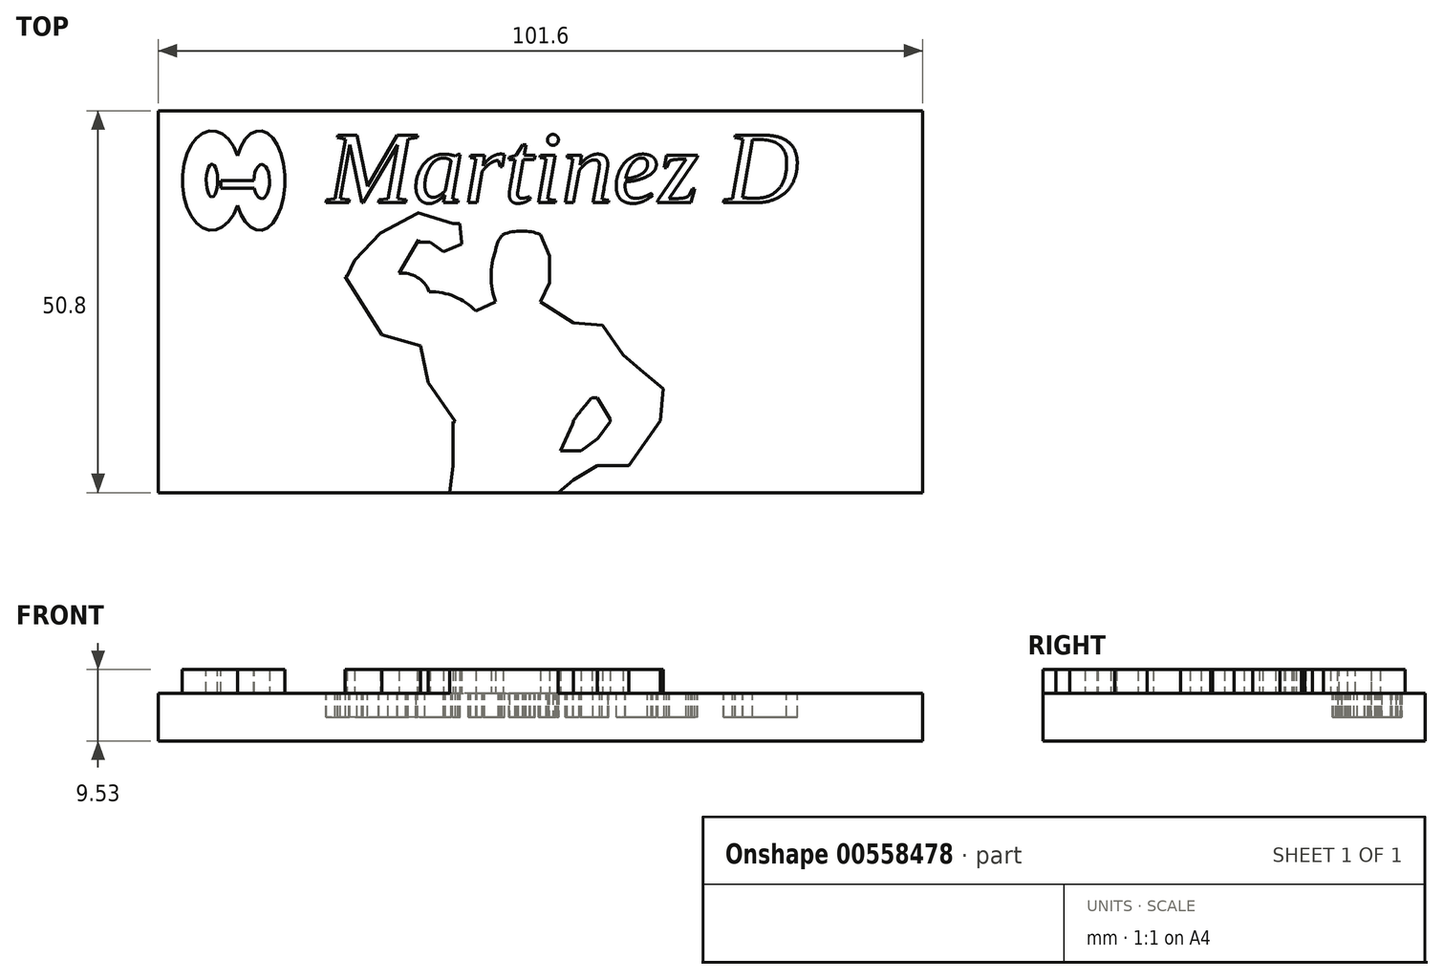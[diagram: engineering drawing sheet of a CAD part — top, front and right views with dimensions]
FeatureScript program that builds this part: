
annotation { "Feature Type Name" : "Feature", "Feature Type Description" : "" }
export const myFeature = defineFeature(function(context is Context, id is Id, definition is map)
    precondition{}
    {
        {
            var Q0;
            Q0=qCreatedBy(makeId("Top.planeOp"),FACE);
            var sketch = newSketch(context, id + "F0", { "sketchPlane" : qUnion([Q0])});
            skLineSegment(sketch, "E0.top", {"start": v(50.8, -25.4) * mm, "end": v(-50.8, -25.4) * mm});
            skLineSegment(sketch, "E0.left", {"start": v(50.8, 25.4) * mm, "end": v(50.8, -25.4) * mm});
            skLineSegment(sketch, "E0.right", {"start": v(-50.8, 25.4) * mm, "end": v(-50.8, -25.4) * mm});
            skPoint(sketch, "E0.middle", {"position": v(0, 0) * mm});
            skLineSegment(sketch, "E1", {"start": v(-50.8, 25.4) * mm, "end": v(29.22, 25.4) * mm});
            skLineSegment(sketch, "E2", {"start": v(29.22, 25.4) * mm, "end": v(50.8, 25.4) * mm});
            skSolve(sketch);
        }
        {
            var Q0;
            Q0=makeQuery(id+"F0.imprint","IMPRINT",FACE,{"disambiguationData":[TD([[makeQuery(id+"F0.imprint","IMPRINT",EDGE,{"derivedFrom":sQuery(id+"F0.wireOp",EDGE,"E0.top")}),-1.0]])]});
            extrude(context, id + "F1", {"entities" : qUnion([Q0]), "depth" : 6.35 * mm, "offsetDistance" : 25.4 * mm});
        }
        {
            var Q0;
            Q0=makeQuery(id+"F1.opExtrude","CAP_FACE",FACE,{"disambiguationData":[OSD([sQuery(id+"F0.wireOp",EDGE,"E0.top"),sQuery(id+"F0.wireOp",EDGE,"E0.left"),sQuery(id+"F0.wireOp",EDGE,"E0.right"),sQuery(id+"F0.wireOp",EDGE,"E1"),sQuery(id+"F0.wireOp",EDGE,"E2")])],"isStart":false});
            var sketch = newSketch(context, id + "F2", { "sketchPlane" : qUnion([Q0])});
            skPoint(sketch, "E3.centerSnap0", {"position": v(-40.78, 16.13) * mm});
            skPoint(sketch, "E3.center.orphan", {"position": v(-37.34, 16.13) * mm});
            skEllipticalArc(sketch, "E4", {});
            skEllipticalArc(sketch, "E5", {});
            skEllipse(sketch, "E6", {"center": v(-43.67, 16.13) * mm, "majorRadius": 4.6 * mm, "minorRadius": 1.55 * mm, "majorAxis": v(0, -1)});
            skEllipse(sketch, "E7", {"center": v(-37.34, 16.13) * mm, "majorRadius": 4.03 * mm, "minorRadius": 1.4 * mm, "majorAxis": v(0, -1)});
            const initialGuessF2  = {"E4": [-0.04366867616772652, 0.016128746792674065, 0, -1, 0.006619533523917198, 0.00393258710358012, 2.0939321384810903, 1.0476605151087033], "E5": [-0.03733694925904274, 0.016128746792674065, 0, -1, 0.006619533523917198, 0.003376708431436235, 5.235524792070883, 4.189253168698496]};
            skSetInitialGuess(sketch, initialGuessF2);
            skSolve(sketch);
        }
        {
            var Q0;
            Q0=makeQuery(id+"F2.imprint","IMPRINT",FACE,{"disambiguationData":[TD([[makeQuery(id+"F2.imprint","IMPRINT",EDGE,{"derivedFrom":sQuery(id+"F2.wireOp",EDGE,"E6")}),-1.0]])]});
            var Q1;
            Q1=makeQuery(id+"F2.imprint","IMPRINT",FACE,{"disambiguationData":[TD([[makeQuery(id+"F2.imprint","IMPRINT",EDGE,{"derivedFrom":sQuery(id+"F2.wireOp",EDGE,"E7")}),-1.0]])]});
            var Q2;
            Q2=makeQuery(id+"F2.imprint","IMPRINT",FACE,{"disambiguationData":[TD([[makeQuery(id+"F2.imprint","IMPRINT",EDGE,{"derivedFrom":sQuery(id+"F2.wireOp",EDGE,"E7")}),1.0]])]});
            var Q3;
            Q3=makeQuery(id+"F2.imprint","IMPRINT",FACE,{"disambiguationData":[TD([[makeQuery(id+"F2.imprint","IMPRINT",EDGE,{"derivedFrom":sQuery(id+"F2.wireOp",EDGE,"E6")}),1.0]])]});
            extrude(context, id + "F3", {"entities" : qUnion([Q0, Q1, Q2, Q3]), "operationType" : NewBodyOperationType.ADD, "depth" : 3.17 * mm, "offsetDistance" : 25.4 * mm});
        }
        {
            var Q0;
            Q0=makeQuery(id+"F3.opExtrude","CAP_FACE",FACE,{"disambiguationData":[OSD([sQuery(id+"F2.wireOp",EDGE,"E4"),sQuery(id+"F2.wireOp",EDGE,"E5")])],"isStart":false});
            var sketch = newSketch(context, id + "F4", { "sketchPlane" : qUnion([Q0])});
            skEllipse(sketch, "E8", {"center": v(-43.67, 16.13) * mm, "majorRadius": 2.17 * mm, "minorRadius": 0.76 * mm, "majorAxis": v(0, -1)});
            skEllipse(sketch, "E9", {"center": v(-37.05, 15.99) * mm, "majorRadius": 2.27 * mm, "minorRadius": 1.05 * mm, "majorAxis": v(0, -1)});
            skSolve(sketch);
        }
        {
            var Q0;
            Q0=makeQuery(id+"F4.imprint","IMPRINT",FACE,{"disambiguationData":[TD([[makeQuery(id+"F4.imprint","IMPRINT",EDGE,{"derivedFrom":sQuery(id+"F4.wireOp",EDGE,"E9")}),1.0]])]});
            var Q1;
            Q1=makeQuery(id+"F4.imprint","IMPRINT",FACE,{"disambiguationData":[TD([[makeQuery(id+"F4.imprint","IMPRINT",EDGE,{"derivedFrom":sQuery(id+"F4.wireOp",EDGE,"E8")}),1.0]])]});
            extrude(context, id + "F5", {"entities" : qUnion([Q0, Q1]), "operationType" : NewBodyOperationType.REMOVE, "oppositeDirection" : true, "depth" : 3.17 * mm, "offsetDistance" : 25.4 * mm});
        }
        {
            var Q0;
            Q0=makeQuery(id+"F3.opExtrude","CAP_FACE",FACE,{"disambiguationData":[OSD([sQuery(id+"F2.wireOp",EDGE,"E4"),sQuery(id+"F2.wireOp",EDGE,"E5")])],"isStart":false});
            var sketch = newSketch(context, id + "F6", { "sketchPlane" : qUnion([Q0])});
            skLineSegment(sketch, "E10.bottom", {"start": v(-42.91, 16.13) * mm, "end": v(-38.02, 16.13) * mm});
            skLineSegment(sketch, "E10.top", {"start": v(-42.91, 15.09) * mm, "end": v(-38.02, 15.09) * mm});
            skLineSegment(sketch, "E10.right", {"start": v(-38.02, 16.13) * mm, "end": v(-38.02, 15.09) * mm});
            skLineSegment(sketch, "E11", {"start": v(-42.5, 16.13) * mm, "end": v(-42.5, 15.09) * mm});
            skSolve(sketch);
        }
        {
            var Q0;
            {var subQ0=sQuery(id+"F6.wireOp",EDGE,"E11");Q0=makeQuery(id+"F6.imprint","IMPRINT",FACE,{"disambiguationData":[TD([[makeQuery(id+"F6.imprint","IMPRINT",EDGE,{"derivedFrom":subQ0}),1.0]])]});}
            extrude(context, id + "F7", {"entities" : qUnion([Q0]), "operationType" : NewBodyOperationType.REMOVE, "oppositeDirection" : true, "depth" : 3.17 * mm, "offsetDistance" : 25.4 * mm});
        }
        {
            var Q0;
            Q0=makeQuery(id+"F1.opExtrude","CAP_FACE",FACE,{"disambiguationData":[OSD([sQuery(id+"F0.wireOp",EDGE,"E0.top"),sQuery(id+"F0.wireOp",EDGE,"E0.left"),sQuery(id+"F0.wireOp",EDGE,"E0.right"),sQuery(id+"F0.wireOp",EDGE,"E1"),sQuery(id+"F0.wireOp",EDGE,"E2")])],"isStart":false});
            var sketch = newSketch(context, id + "F8", { "sketchPlane" : qUnion([Q0])});
            skText(sketch, "E12", { "text": "Martinez D ", "fontName": "Tinos-Italic.ttf"});
            const initialGuessF8  = {"E12": [-0.02836, 0.0132, 1, 0, 0.00985]};
            skSetInitialGuess(sketch, initialGuessF8);
            skSolve(sketch);
        }
        {
            var Q0;
            Q0 = qSketchRegion(id + "F8", true);
            extrude(context, id + "F9", {"entities" : qUnion([Q0]), "operationType" : NewBodyOperationType.REMOVE, "oppositeDirection" : true, "depth" : 3.17 * mm, "offsetDistance" : 25.4 * mm});
        }
        {
            var Q0;
            {var subQ0=sQuery(id+"F0.wireOp",EDGE,"E2");var subQ1=sQuery(id+"F0.wireOp",EDGE,"E1");var subQ2=sQuery(id+"F0.wireOp",EDGE,"E0.right");var subQ3=sQuery(id+"F0.wireOp",EDGE,"E0.left");var subQ4=sQuery(id+"F0.wireOp",EDGE,"E0.top");Q0=makeQuery(id+"F9.boolean.opBoolean","SPLIT",FACE,{"disambiguationData":[TD([makeQuery(id+"F1.opExtrude","SWEPT_FACE",FACE,{"disambiguationData":[OSD([subQ4])]})])],"derivedFrom":makeQuery(id+"F1.opExtrude","CAP_FACE",FACE,{"disambiguationData":[OSD([subQ4,subQ3,subQ2,subQ1,subQ0])],"isStart":false})});}
            var sketch = newSketch(context, id + "F10", { "sketchPlane" : qUnion([Q0])});
            skArc(sketch, "E13", {"start": v(-14.77, 1.35) * mm, "mid": v(-16.37, 3.25) * mm, "end": v(-18.8, 3.8) * mm});
            skArc(sketch, "E14", {"start": v(-8.58, -1.24) * mm, "mid": v(-11.4, 0.7) * mm, "end": v(-14.77, 1.35) * mm});
            skPoint(sketch, "E15.1.internal.orphan", {"position": v(-6, 0) * mm});
            skArc(sketch, "E16", {"start": v(-6, 6.82) * mm, "mid": v(-6.55, 3.4) * mm, "end": v(-6, 0) * mm});
            skArc(sketch, "E17", {"start": v(-4.99, 8.97) * mm, "mid": v(-5.63, 7.96) * mm, "end": v(-6, 6.82) * mm});
            skPoint(sketch, "E18.end.orphan", {"position": v(0, 8.97) * mm});
            skArc(sketch, "E19", {"start": v(0, 8.97) * mm, "mid": v(-2.5, 9.4) * mm, "end": v(-4.99, 8.97) * mm});
            skFitSpline(sketch, "E20", {"points": [v(-12.04, -25.4) * mm, v(-11.6, -21.82) * mm], "startDerivative": vector(0.43, 3.58) * mm, "endDerivative": vector(0.43, 3.58) * mm});
            skFitSpline(sketch, "E21", {"points": [v(-11.6, -21.82) * mm, v(-11.6, -15.92) * mm], "startDerivative": vector(0, 5.9) * mm, "endDerivative": vector(0, 5.9) * mm});
            skFitSpline(sketch, "E22", {"points": [v(-11.32, -15.92) * mm, v(-14.91, -10.74) * mm], "startDerivative": vector(-3.6, 5.18) * mm, "endDerivative": vector(-3.6, 5.18) * mm});
            skFitSpline(sketch, "E23", {"points": [v(-14.91, -10.74) * mm, v(-15.92, -5.85) * mm], "startDerivative": vector(-1, 4.9) * mm, "endDerivative": vector(-1, 4.9) * mm});
            skFitSpline(sketch, "E24", {"points": [v(-15.92, -5.85) * mm, v(-21.1, -4.4) * mm], "startDerivative": vector(-5.18, 1.44) * mm, "endDerivative": vector(-5.18, 1.44) * mm});
            skFitSpline(sketch, "E25", {"points": [v(-21.1, -4.4) * mm, v(-25.99, 3.36) * mm], "startDerivative": vector(-4.88, 7.77) * mm, "endDerivative": vector(-4.88, 7.77) * mm});
            skFitSpline(sketch, "E26", {"points": [v(-25.7, 3.36) * mm, v(-24.7, 5.52) * mm], "startDerivative": vector(1, 2.16) * mm, "endDerivative": vector(1, 2.16) * mm});
            skFitSpline(sketch, "E27", {"points": [v(-24.7, 5.52) * mm, v(-21.25, 9.12) * mm], "startDerivative": vector(3.45, 3.6) * mm, "endDerivative": vector(3.45, 3.6) * mm});
            skFitSpline(sketch, "E28", {"points": [v(-21.25, 9.12) * mm, v(-16.35, 11.75) * mm], "startDerivative": vector(4.9, 2.63) * mm, "endDerivative": vector(4.9, 2.63) * mm});
            skFitSpline(sketch, "E29", {"points": [v(-16.35, 11.85) * mm, v(-11.6, 10.41) * mm], "startDerivative": vector(4.75, -1.44) * mm, "endDerivative": vector(4.75, -1.44) * mm});
            skFitSpline(sketch, "E30", {"points": [v(-10.74, 10.41) * mm, v(-10.45, 7.92) * mm], "startDerivative": vector(0.29, -2.5) * mm, "endDerivative": vector(0.29, -2.5) * mm});
            skFitSpline(sketch, "E31", {"points": [v(-10.45, 7.68) * mm, v(-12.9, 6.67) * mm], "startDerivative": vector(-2.45, -1) * mm, "endDerivative": vector(-2.45, -1) * mm});
            skFitSpline(sketch, "E32", {"points": [v(-12.9, 6.67) * mm, v(-14.66, 7.92) * mm], "startDerivative": vector(-1.76, 1.25) * mm, "endDerivative": vector(-1.76, 1.25) * mm});
            skFitSpline(sketch, "E33", {"points": [v(-14.66, 7.92) * mm, v(-16.2, 7.92) * mm], "startDerivative": vector(-1.55, 0) * mm, "endDerivative": vector(-1.55, 0) * mm});
            skFitSpline(sketch, "E34", {"points": [v(-16.2, 8.25) * mm, v(-18.8, 3.8) * mm], "startDerivative": vector(-2.6, -4.46) * mm, "endDerivative": vector(-2.6, -4.46) * mm});
            skFitSpline(sketch, "E35", {"points": [v(16.3, -11.55) * mm, v(13.3, -9.01) * mm], "startDerivative": vector(-3.02, 2.53) * mm, "endDerivative": vector(-3.02, 2.53) * mm});
            skFitSpline(sketch, "E36", {"points": [v(13.3, -9.01) * mm, v(10.99, -7.08) * mm], "startDerivative": vector(-2.3, 1.93) * mm, "endDerivative": vector(-2.3, 1.93) * mm});
            skFitSpline(sketch, "E37", {"points": [v(10.99, -7.08) * mm, v(8.25, -3.11) * mm], "startDerivative": vector(-2.73, 3.97) * mm, "endDerivative": vector(-2.73, 3.97) * mm});
            skFitSpline(sketch, "E38", {"points": [v(8.25, -3.11) * mm, v(4.37, -2.83) * mm], "startDerivative": vector(-3.89, 0.29) * mm, "endDerivative": vector(-3.89, 0.29) * mm});
            skFitSpline(sketch, "E39", {"points": [v(4.37, -2.83) * mm, v(0, 0) * mm], "startDerivative": vector(-4.37, 2.83) * mm, "endDerivative": vector(-4.37, 2.83) * mm});
            skFitSpline(sketch, "E40", {"points": [v(0, 0) * mm, v(1.2, 2.5) * mm], "startDerivative": vector(1.2, 2.5) * mm, "endDerivative": vector(1.2, 2.5) * mm});
            skFitSpline(sketch, "E41", {"points": [v(1.2, 2.5) * mm, v(1.2, 5.66) * mm], "startDerivative": vector(0, 3.17) * mm, "endDerivative": vector(0, 3.17) * mm});
            skFitSpline(sketch, "E42", {"points": [v(1.2, 6.1) * mm, v(0, 8.97) * mm], "startDerivative": vector(-1.2, 2.88) * mm, "endDerivative": vector(-1.2, 2.88) * mm});
            skFitSpline(sketch, "E43", {"points": [v(11.76, -21.82) * mm, v(15.95, -15.85) * mm], "startDerivative": vector(4.2, 5.97) * mm, "endDerivative": vector(4.2, 5.97) * mm});
            skFitSpline(sketch, "E44", {"points": [v(16.3, -11.55) * mm, v(15.95, -15.85) * mm], "startDerivative": vector(-0.36, -4.3) * mm, "endDerivative": vector(-0.36, -4.3) * mm});
            skFitSpline(sketch, "E45", {"points": [v(11.76, -21.82) * mm, v(7.53, -21.82) * mm], "startDerivative": vector(-4.22, 0) * mm, "endDerivative": vector(-4.22, 0) * mm});
            skFitSpline(sketch, "E46", {"points": [v(7.53, -21.82) * mm, v(4.37, -23.7) * mm], "startDerivative": vector(-3.17, -1.87) * mm, "endDerivative": vector(-3.17, -1.87) * mm});
            skFitSpline(sketch, "E47", {"points": [v(4.37, -23.7) * mm, v(2.35, -25.4) * mm], "startDerivative": vector(-2.01, -1.7) * mm, "endDerivative": vector(-2.01, -1.7) * mm});
            skFitSpline(sketch, "E48", {"points": [v(2.64, -19.83) * mm, v(5.42, -19.83) * mm], "startDerivative": vector(2.78, 0) * mm, "endDerivative": vector(2.78, 0) * mm});
            skFitSpline(sketch, "E49", {"points": [v(5.42, -19.83) * mm, v(7.53, -18.23) * mm], "startDerivative": vector(2.11, 1.6) * mm, "endDerivative": vector(2.11, 1.6) * mm});
            skFitSpline(sketch, "E50", {"points": [v(7.68, -18.08) * mm, v(9.26, -15.92) * mm], "startDerivative": vector(1.58, 2.16) * mm, "endDerivative": vector(1.58, 2.16) * mm});
            skFitSpline(sketch, "E51", {"points": [v(9.26, -15.63) * mm, v(7.53, -12.76) * mm], "startDerivative": vector(-1.73, 2.88) * mm, "endDerivative": vector(-1.73, 2.88) * mm});
            skFitSpline(sketch, "E52", {"points": [v(7.53, -12.76) * mm, v(5.42, -12.76) * mm], "startDerivative": vector(-2.11, 0) * mm, "endDerivative": vector(-2.11, 0) * mm});
            skFitSpline(sketch, "E53", {"points": [v(6.83, -12.76) * mm, v(4.37, -15.85) * mm, v(4.37, -15.92) * mm], "startDerivative": vector(-4.02, -4.8) * mm, "endDerivative": vector(0.17, -0.43) * mm});
            skFitSpline(sketch, "E54", {"points": [v(4.22, -16.35) * mm, v(2.64, -19.83) * mm], "startDerivative": vector(-1.58, -3.48) * mm, "endDerivative": vector(-1.58, -3.48) * mm});
            skLineSegment(sketch, "E55", {"start": v(-8.58, -1.24) * mm, "end": v(-6, 0) * mm});
            skLineSegment(sketch, "E56", {"start": v(2.35, -25.4) * mm, "end": v(-12.04, -25.4) * mm});
            skLineSegment(sketch, "E57", {"start": v(9.26, -15.63) * mm, "end": v(9.26, -15.92) * mm});
            skLineSegment(sketch, "E58", {"start": v(4.37, -15.92) * mm, "end": v(4.22, -16.35) * mm});
            skLineSegment(sketch, "E59", {"start": v(-10.74, 10.41) * mm, "end": v(-11.6, 10.41) * mm});
            skLineSegment(sketch, "E60", {"start": v(-16.2, 8.25) * mm, "end": v(-16.2, 7.92) * mm});
            skLineSegment(sketch, "E61", {"start": v(1.2, 6.1) * mm, "end": v(1.2, 5.66) * mm});
            skLineSegment(sketch, "E62", {"start": v(-10.45, 7.92) * mm, "end": v(-10.45, 7.68) * mm});
            skLineSegment(sketch, "E63", {"start": v(-6, 6.82) * mm, "end": v(-6, 6.82) * mm});
            skPoint(sketch, "E64.end.orphan", {"position": v(16.47, -18.23) * mm});
            skLineSegment(sketch, "E65", {"start": v(-11.6, -15.92) * mm, "end": v(-11.32, -15.92) * mm});
            skLineSegment(sketch, "E66", {"start": v(7.68, -18.08) * mm, "end": v(7.53, -18.23) * mm});
            skLineSegment(sketch, "E67", {"start": v(-25.99, 3.36) * mm, "end": v(-25.7, 3.36) * mm});
            skLineSegment(sketch, "E68", {"start": v(4.37, -15.92) * mm, "end": v(4.37, -15.85) * mm});
            skLineSegment(sketch, "E69", {"start": v(4.22, -16.35) * mm, "end": v(4.45, -15.7) * mm});
            skLineSegment(sketch, "E70", {"start": v(-12.04, -25.4) * mm, "end": v(2.35, -25.4) * mm});
            skLineSegment(sketch, "E71", {"start": v(-16.35, 11.85) * mm, "end": v(-16.35, 11.75) * mm});
            skSolve(sketch);
        }
        {
            var Q0;
            Q0=makeQuery(id+"F10.imprint","IMPRINT",FACE,{"disambiguationData":[TD([[makeQuery(id+"F10.imprint","IMPRINT",EDGE,{"derivedFrom":sQuery(id+"F10.wireOp",EDGE,"E13")}),1.0]])]});
            extrude(context, id + "F11", {"entities" : qUnion([Q0]), "operationType" : NewBodyOperationType.ADD, "depth" : 3.17 * mm, "offsetDistance" : 25.4 * mm});
        }
    });
